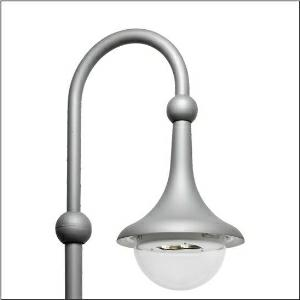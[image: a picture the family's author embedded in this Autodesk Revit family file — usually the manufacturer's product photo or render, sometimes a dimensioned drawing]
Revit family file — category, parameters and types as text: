
# Revit family: grosse_glocke_iq___st1_2a_5xa1565m1f108_263f
name_source: partatom
category: Lighting Fixtures
units: mm (PartAtom-declared; Revit-internal decimal feet)

## family parameters
Cut with Voids When Loaded = No
Host = Face
Light Source = No
Part Type = Normal
Room Calculation Point = No
Round Connector Dimension = Use Diameter
Shared = No

## types (1)
- --- (1 x LED, 4470 lm, 34.3 W, 2700K)
    Apparent Load = 34 VA
    CIE Flux Codes = 28 66 95 100 100
    Color Rendering = 70
    Color Temperature = 2700K
    Default Elevation = 1800 mm
    Description = Large Bell iQ, mast luminaire, primary light control with 3 zone facetted reflector, of plastic, silver coated, primary optical cover: enclosure, of PMMA, transparent, light distribution: ST1.2a, light emission: direct distribution, primary light characteristic: asymmetric, installation type: suspended mounting, High Power LED, rated luminous flux: 4.470lm, luminous efficacy: 130lm/W, light colour: 727, colour temperature: 2700K, control gear: iQ Street-Remote, control: optimised constant luminous flux control (CLO 2.0), Desk-Remote (wireless, voltage-free reading and setting of iQ features in the workshop via application-optimized NFC function/RFID function), Light-Fading, Smart-Wire, Night-Set, Lumen-Switch, Temp-Guard, Auto-Match, Street-Remote, pre-setting: logarithmic dimming characteristic, mains connection: 230..240V, AC, 50/60Hz, start of lifetime: 34W, end of service life: 38W, reduction: 16W, luminaire housing, bell-shaped, of glass-fibre reinforced polyester, coated, Siteco® metallic grey (DB 702S), please order curved mast extension separately, diameter: 530mm, height: 695mm, mounting height: 4..6m, protection rating (complete): IP54, insulation class (complete): insulation class II (safety insulation), certification: CE, ENEC, VDE, impact resistance: IK08, standard-compliant lighting for roads and squares, packaging unit: 1 piece

Light Distribution: ST1.2a
    Height = 695 mm
    Lamp = 1 x LED
    Lamp Light Flux = 4470 lm
    Lamp Power = 34.3 W
    Lamp count = 1
    Length = 530 mm
    Luminous efficacy = 130 lm/W
    Manufacturer = Siteco
    ModVariant = No
    Model = 5XA1565M1F108
    Number of Poles = 1
    OnlyDefault = Yes
    Power Factor = 1
    Product Name = Große Glocke iQ | ST1.2a
    Product group = mast luminaire | pylon annexe
    ProductGroupID = 6200
    Protection Class = Protection class II
    Protection Degree = IP 54
    RLX_Detail_Level = 1
    RLX_Emergency_Light_Flux = 0 lm
    RLX_Emergency_Type = 0
    RLX_Emergency_Type_DB = No
    RlxData = <blob elided: 71737 chars, md5=ccff7f2e>
    Socket = socket
    Standby Power = 0 W
    System Light Flux = 4470 lm
    System Power = 34 W
    Type Comments = factory setting: luminous flux: 100 % | dim-lin: 254 | 640 mA
    Type Image = l_1347688.jpg
    URL = http://relux.com
    VarID = @adj_079981
    Voltage = 0 V
    Weight = 0.00 kg
    Width = 0 mm  [stored 0 ft]

note: [stored X ft] marks values corroborated as IEEE doubles in the binary element streams (Revit-internal decimal feet)

## geometry (parser evidence)
native form markers: Blend x4, Sweep x9
no freeform markers — native parametric forms only
